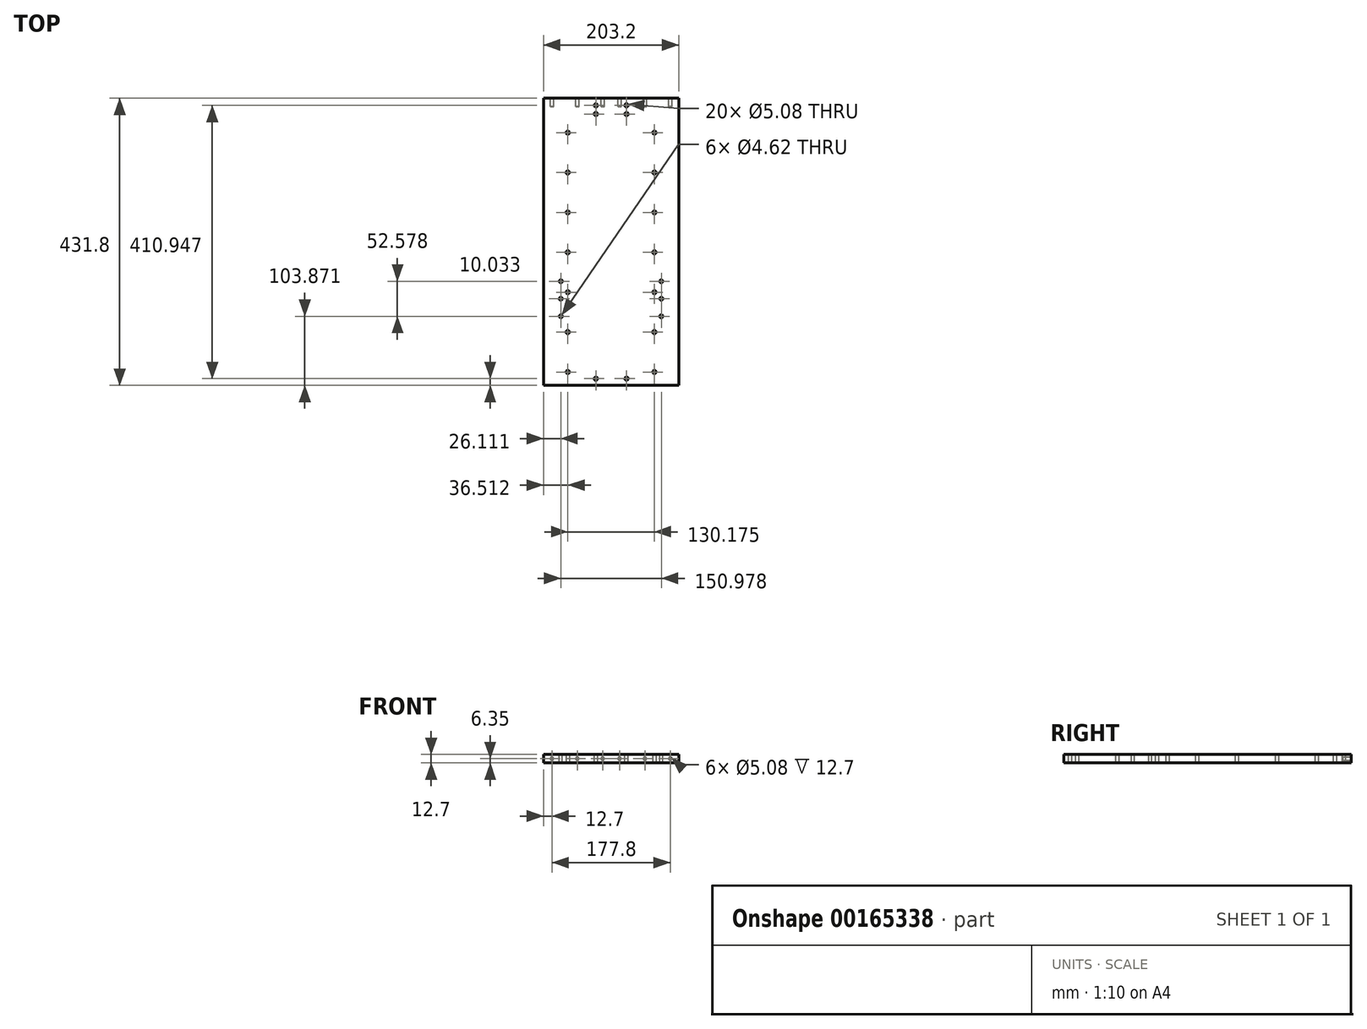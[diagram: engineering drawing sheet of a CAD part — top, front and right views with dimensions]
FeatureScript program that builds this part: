
annotation { "Feature Type Name" : "Feature", "Feature Type Description" : "" }
export const myFeature = defineFeature(function(context is Context, id is Id, definition is map)
    precondition{}
    {
        {
            var Q0;
            Q0=qCreatedBy(makeId("Top.planeOp"),FACE);
            var sketch = newSketch(context, id + "F0", { "sketchPlane" : qUnion([Q0])});
            skLineSegment(sketch, "E0.rect.bottom", {"start": v(101.6, -215.9) * mm, "end": v(-101.6, -215.9) * mm});
            skLineSegment(sketch, "E0.rect.top", {"start": v(101.6, 215.9) * mm, "end": v(-101.6, 215.9) * mm});
            skLineSegment(sketch, "E0.rect.left", {"start": v(101.6, -215.9) * mm, "end": v(101.6, 215.9) * mm});
            skLineSegment(sketch, "E0.rect.right", {"start": v(-101.6, -215.9) * mm, "end": v(-101.6, 215.9) * mm});
            skPoint(sketch, "E0.rect.middle", {"position": v(0, 0) * mm});
            skLineSegment(sketch, "E1", {"start": v(-65.09, 215.9) * mm, "end": v(-65.09, -215.9) * mm, "construction": true});
            skLineSegment(sketch, "E2", {"start": v(65.09, 215.9) * mm, "end": v(65.09, -215.9) * mm, "construction": true});
            skLineSegment(sketch, "E3", {"start": v(-101.6, -195.83) * mm, "end": v(101.6, -195.83) * mm, "construction": true});
            skLineSegment(sketch, "E4", {"start": v(-101.6, -135.84) * mm, "end": v(101.6, -135.84) * mm, "construction": true});
            skLineSegment(sketch, "E5", {"start": v(-101.6, -75.84) * mm, "end": v(101.6, -75.84) * mm, "construction": true});
            skLineSegment(sketch, "E6", {"start": v(101.6, -75.84) * mm, "end": v(98.14, -81.1) * mm, "construction": true});
            skLineSegment(sketch, "E7", {"start": v(-101.6, -15.85) * mm, "end": v(101.6, -15.85) * mm, "construction": true});
            skPoint(sketch, "E7.endSnap0", {"position": v(101.6, 0) * mm});
            skLineSegment(sketch, "E8", {"start": v(101.6, -15.85) * mm, "end": v(98.56, -15.85) * mm, "construction": true});
            skLineSegment(sketch, "E9", {"start": v(-101.6, 44.15) * mm, "end": v(101.6, 44.15) * mm, "construction": true});
            skCircle(sketch, "E10", {"center": v(-65.09, -195.83) * mm, "radius": 2.54 * mm});
            skCircle(sketch, "E11", {"center": v(-65.09, -135.84) * mm, "radius": 2.54 * mm});
            skCircle(sketch, "E12", {"center": v(-65.09, -75.84) * mm, "radius": 2.54 * mm});
            skCircle(sketch, "E13", {"center": v(-65.09, -15.85) * mm, "radius": 2.54 * mm});
            skCircle(sketch, "E14", {"center": v(-65.09, 44.15) * mm, "radius": 2.54 * mm});
            skCircle(sketch, "E15", {"center": v(65.09, 44.15) * mm, "radius": 2.54 * mm});
            skCircle(sketch, "E16", {"center": v(65.09, -15.85) * mm, "radius": 2.54 * mm});
            skCircle(sketch, "E17", {"center": v(65.09, -75.84) * mm, "radius": 2.54 * mm});
            skCircle(sketch, "E18", {"center": v(65.09, -135.84) * mm, "radius": 2.54 * mm});
            skCircle(sketch, "E19", {"center": v(65.09, -195.83) * mm, "radius": 2.54 * mm});
            skLineSegment(sketch, "E20", {"start": v(-101.6, 104.14) * mm, "end": v(101.6, 104.14) * mm, "construction": true});
            skLineSegment(sketch, "E21", {"start": v(-101.6, 164.13) * mm, "end": v(101.6, 164.13) * mm, "construction": true});
            skCircle(sketch, "E22", {"center": v(-65.09, 104.14) * mm, "radius": 2.54 * mm});
            skCircle(sketch, "E23", {"center": v(-65.09, 164.13) * mm, "radius": 2.54 * mm});
            skCircle(sketch, "E24", {"center": v(65.09, 164.13) * mm, "radius": 2.54 * mm});
            skCircle(sketch, "E25", {"center": v(65.09, 104.14) * mm, "radius": 2.54 * mm});
            skSolve(sketch);
        }
        {
            var Q0;
            Q0=qSketchRegion(id+"F0",true);
            extrude(context, id + "F1", {"entities" : qUnion([Q0]), "depth" : 12.7 * mm});
        }
        {
            var Q0;
            Q0=makeQuery(id+"F1.opExtrude","CAP_FACE",FACE,{"disambiguationData":[OSD([sQuery(id+"F0.wireOp",EDGE,"E0.rect.bottom"),sQuery(id+"F0.wireOp",EDGE,"E0.rect.top"),sQuery(id+"F0.wireOp",EDGE,"E0.rect.left"),sQuery(id+"F0.wireOp",EDGE,"E0.rect.right"),sQuery(id+"F0.wireOp",EDGE,"E10"),sQuery(id+"F0.wireOp",EDGE,"E11"),sQuery(id+"F0.wireOp",EDGE,"E12"),sQuery(id+"F0.wireOp",EDGE,"E13"),sQuery(id+"F0.wireOp",EDGE,"E14"),sQuery(id+"F0.wireOp",EDGE,"E15"),sQuery(id+"F0.wireOp",EDGE,"E16"),sQuery(id+"F0.wireOp",EDGE,"E17"),sQuery(id+"F0.wireOp",EDGE,"E18"),sQuery(id+"F0.wireOp",EDGE,"E19"),sQuery(id+"F0.wireOp",EDGE,"7b17098a-9bc7-4356-bacf-ebf9c2cc2035"),sQuery(id+"F0.wireOp",EDGE,"7bd67d0a-61c6-4c01-8da3-961ec9462f9d")])],"isStart":false});
            var sketch = newSketch(context, id + "F2", { "sketchPlane" : qUnion([Q0])});
            skLineSegment(sketch, "E26", {"start": v(-101.6, 205.08) * mm, "end": v(101.6, 205.08) * mm, "construction": true});
            skLineSegment(sketch, "E27", {"start": v(-101.6, 192.05) * mm, "end": v(101.6, 192.05) * mm, "construction": true});
            skLineSegment(sketch, "E28", {"start": v(101.6, 203.44) * mm, "end": v(101.82, 201.04) * mm, "construction": true});
            skLineSegment(sketch, "E29", {"start": v(-22.86, 215.9) * mm, "end": v(-22.86, -215.9) * mm, "construction": true});
            skLineSegment(sketch, "E30", {"start": v(23.14, 215.9) * mm, "end": v(23.14, -215.9) * mm, "construction": true});
            skCircle(sketch, "E31", {"center": v(-22.86, 192.05) * mm, "radius": 2.54 * mm});
            skCircle(sketch, "E32", {"center": v(-22.86, 205.08) * mm, "radius": 2.54 * mm});
            skCircle(sketch, "E33", {"center": v(23.14, 205.08) * mm, "radius": 2.54 * mm});
            skCircle(sketch, "E34", {"center": v(23.14, 192.05) * mm, "radius": 2.54 * mm});
            skCircle(sketch, "E35", {"center": v(-22.86, -205.87) * mm, "radius": 2.54 * mm});
            skCircle(sketch, "E36", {"center": v(23.14, -205.87) * mm, "radius": 2.54 * mm});
            skSolve(sketch);
        }
        {
            var Q0;
            Q0=qSketchRegion(id+"F2",true);
            extrude(context, id + "F3", {"entities" : qUnion([Q0]), "operationType" : NewBodyOperationType.REMOVE, "endBound" : BoundingType.THROUGH_ALL, "oppositeDirection" : true, "depth" : 25.4 * mm});
        }
        {
            var Q0;
            Q0=makeQuery(id+"F1.opExtrude","SWEPT_FACE",FACE,{"disambiguationData":[OSD([sQuery(id+"F0.wireOp",EDGE,"E0.rect.top")])]});
            var sketch = newSketch(context, id + "F4", { "sketchPlane" : qUnion([Q0])});
            skLineSegment(sketch, "E37.bottom", {"start": v(-101.6, 12.7) * mm, "end": v(101.6, 12.7) * mm, "construction": true});
            skLineSegment(sketch, "E37.top", {"start": v(-101.6, 0) * mm, "end": v(101.6, 0) * mm, "construction": true});
            skLineSegment(sketch, "E37.left", {"start": v(-101.6, 12.7) * mm, "end": v(-101.6, 0) * mm, "construction": true});
            skLineSegment(sketch, "E37.right", {"start": v(101.6, 12.7) * mm, "end": v(101.6, 0) * mm, "construction": true});
            skLineSegment(sketch, "E38", {"start": v(-50.8, 12.7) * mm, "end": v(-50.8, 0) * mm, "construction": true});
            skLineSegment(sketch, "E39", {"start": v(50.8, 12.7) * mm, "end": v(50.8, 0) * mm, "construction": true});
            skLineSegment(sketch, "E40", {"start": v(88.9, 12.7) * mm, "end": v(88.9, 0) * mm, "construction": true});
            skLineSegment(sketch, "E41", {"start": v(-88.9, 12.7) * mm, "end": v(-88.9, 0) * mm, "construction": true});
            skLineSegment(sketch, "E42", {"start": v(-101.6, 6.35) * mm, "end": v(101.6, 6.35) * mm, "construction": true});
            skCircle(sketch, "E43", {"center": v(-88.9, 6.35) * mm, "radius": 2.54 * mm});
            skCircle(sketch, "E44", {"center": v(-50.8, 6.35) * mm, "radius": 2.54 * mm});
            skCircle(sketch, "E45", {"center": v(50.8, 6.35) * mm, "radius": 2.54 * mm});
            skCircle(sketch, "E46", {"center": v(88.9, 6.35) * mm, "radius": 2.54 * mm});
            skPoint(sketch, "E47.endSnap0", {"position": v(0, 0) * mm});
            skLineSegment(sketch, "E48", {"start": v(12.7, 0) * mm, "end": v(12.7, 12.7) * mm, "construction": true});
            skLineSegment(sketch, "E49", {"start": v(-12.7, 0) * mm, "end": v(-12.7, 12.7) * mm, "construction": true});
            skCircle(sketch, "E50", {"center": v(12.7, 6.35) * mm, "radius": 2.54 * mm});
            skCircle(sketch, "E51", {"center": v(-12.7, 6.35) * mm, "radius": 2.54 * mm});
            skSolve(sketch);
        }
        {
            var Q0;
            Q0=qSketchRegion(id+"F4",true);
            extrude(context, id + "F5", {"entities" : qUnion([Q0]), "operationType" : NewBodyOperationType.REMOVE, "oppositeDirection" : true, "depth" : 12.7 * mm});
        }
        {
            var Q0;
            Q0=makeQuery(id+"F1.opExtrude","CAP_FACE",FACE,{"disambiguationData":[OSD([sQuery(id+"F0.wireOp",EDGE,"E0.rect.bottom"),sQuery(id+"F0.wireOp",EDGE,"E0.rect.top"),sQuery(id+"F0.wireOp",EDGE,"E0.rect.left"),sQuery(id+"F0.wireOp",EDGE,"E0.rect.right"),sQuery(id+"F0.wireOp",EDGE,"E10"),sQuery(id+"F0.wireOp",EDGE,"E11"),sQuery(id+"F0.wireOp",EDGE,"E12"),sQuery(id+"F0.wireOp",EDGE,"E13"),sQuery(id+"F0.wireOp",EDGE,"E14"),sQuery(id+"F0.wireOp",EDGE,"E15"),sQuery(id+"F0.wireOp",EDGE,"E16"),sQuery(id+"F0.wireOp",EDGE,"E17"),sQuery(id+"F0.wireOp",EDGE,"E18"),sQuery(id+"F0.wireOp",EDGE,"E19"),sQuery(id+"F0.wireOp",EDGE,"E22"),sQuery(id+"F0.wireOp",EDGE,"E23"),sQuery(id+"F0.wireOp",EDGE,"E24"),sQuery(id+"F0.wireOp",EDGE,"E25")])],"isStart":false});
            var sketch = newSketch(context, id + "F6", { "sketchPlane" : qUnion([Q0])});
            skLineSegment(sketch, "E52", {"start": v(-101.6, -125.72) * mm, "end": v(101.6, -125.72) * mm, "construction": true});
            skLineSegment(sketch, "E53", {"start": v(-66.49, -133.72) * mm, "end": v(65.08, -133.3) * mm, "construction": true});
            skLineSegment(sketch, "E54", {"start": v(-101.6, -112.03) * mm, "end": v(101.6, -112.03) * mm, "construction": true});
            skLineSegment(sketch, "E55", {"start": v(-101.6, -85.74) * mm, "end": v(101.6, -85.74) * mm, "construction": true});
            skLineSegment(sketch, "E56", {"start": v(101.6, -85.74) * mm, "end": v(101.88, -87.08) * mm, "construction": true});
            skLineSegment(sketch, "E57", {"start": v(-101.6, -59.45) * mm, "end": v(101.6, -59.45) * mm, "construction": true});
            skLineSegment(sketch, "E58", {"start": v(-101.6, -45.76) * mm, "end": v(101.6, -45.76) * mm, "construction": true});
            skLineSegment(sketch, "E59", {"start": v(0, 0) * mm, "end": v(0, -215.9) * mm, "construction": true});
            skLineSegment(sketch, "E60", {"start": v(-75.49, 215.9) * mm, "end": v(-75.49, -215.9) * mm, "construction": true});
            skLineSegment(sketch, "E61", {"start": v(75.49, 215.9) * mm, "end": v(75.49, -215.9) * mm, "construction": true});
            skCircle(sketch, "E62", {"center": v(-75.49, -59.45) * mm, "radius": 2.31 * mm});
            skCircle(sketch, "E63", {"center": v(-75.49, -85.74) * mm, "radius": 2.31 * mm});
            skCircle(sketch, "E64", {"center": v(-75.49, -112.03) * mm, "radius": 2.31 * mm});
            skCircle(sketch, "E65", {"center": v(75.49, -59.45) * mm, "radius": 2.31 * mm});
            skCircle(sketch, "E66", {"center": v(75.49, -85.74) * mm, "radius": 2.31 * mm});
            skCircle(sketch, "E67", {"center": v(75.49, -112.03) * mm, "radius": 2.31 * mm});
            skSolve(sketch);
        }
        {
            var Q0;
            Q0=qSketchRegion(id+"F6",true);
            extrude(context, id + "F7", {"entities" : qUnion([Q0]), "operationType" : NewBodyOperationType.REMOVE, "oppositeDirection" : true, "depth" : 25.4 * mm});
        }
        {
            var Q0;
            Q0=qSketchRegion(id+"F6",true);
            extrude(context, id + "F8", {"entities" : qUnion([Q0]), "operationType" : NewBodyOperationType.REMOVE, "oppositeDirection" : true, "depth" : 25.4 * mm});
        }
    });
